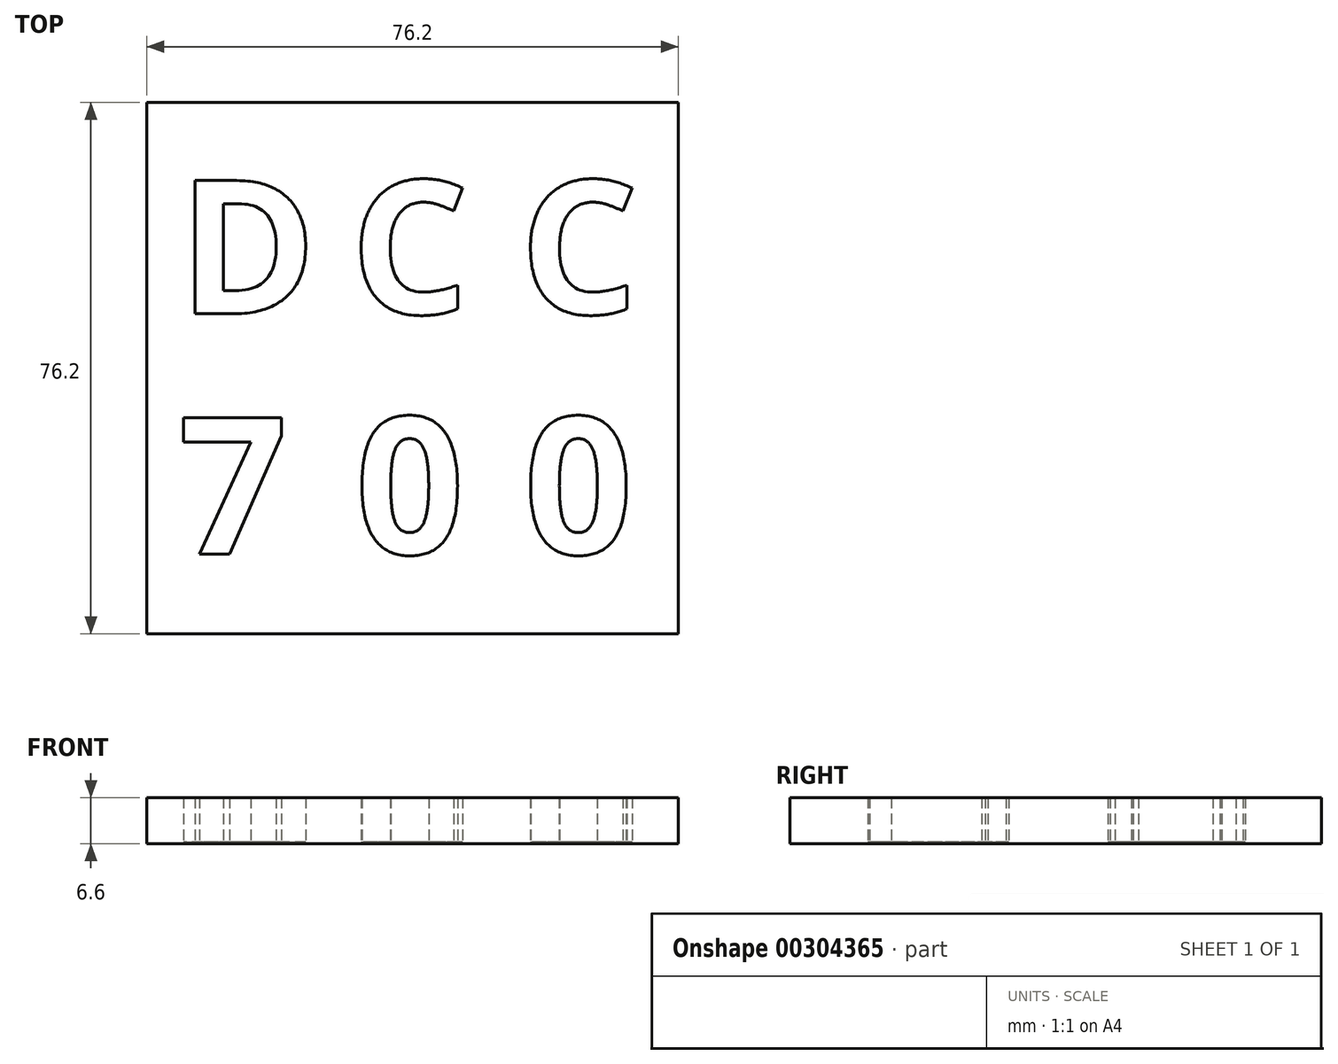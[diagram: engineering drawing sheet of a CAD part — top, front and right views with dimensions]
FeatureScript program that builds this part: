
annotation { "Feature Type Name" : "Feature", "Feature Type Description" : "" }
export const myFeature = defineFeature(function(context is Context, id is Id, definition is map)
    precondition{}
    {
        {
            var Q0;
            Q0=qCreatedBy(makeId("Top.planeOp"),FACE);
            var sketch = newSketch(context, id + "F0", { "sketchPlane" : qUnion([Q0])});
            skLineSegment(sketch, "E0.bottom", {"start": v(-38.1, 38.1) * mm, "end": v(38.1, 38.1) * mm});
            skLineSegment(sketch, "E0.top", {"start": v(-38.1, -38.1) * mm, "end": v(38.1, -38.1) * mm});
            skLineSegment(sketch, "E0.left", {"start": v(-38.1, 38.1) * mm, "end": v(-38.1, -38.1) * mm});
            skLineSegment(sketch, "E0.right", {"start": v(38.1, 38.1) * mm, "end": v(38.1, -38.1) * mm});
            skPoint(sketch, "E0.middle", {"position": v(0, 0) * mm});
            skText(sketch, "E1", { "text": "D\n", "fontName": "OpenSans-Bold.ttf"});
            skText(sketch, "E2", { "text": "C", "fontName": "OpenSans-Bold.ttf"});
            skText(sketch, "E3", { "text": "C\n", "fontName": "OpenSans-Bold.ttf"});
            skText(sketch, "E4", { "text": "7", "fontName": "OpenSans-Bold.ttf"});
            skText(sketch, "E5", { "text": "0", "fontName": "OpenSans-Bold.ttf"});
            skText(sketch, "E6", { "text": "0", "fontName": "OpenSans-Bold.ttf"});
            const initialGuessF0  = {"E1": [-0.03359, 0.00778, 1, 0, 0.01927], "E2": [-0.00892, 0.00778, 1, 0, 0.01927], "E3": [0.01535, 0.00778, 1, 0, 0.01927], "E4": [-0.03359, -0.02666, 1, 0, 0.01976], "E5": [-0.00824, -0.02666, 1, 0, 0.01976], "E6": [0.01594, -0.02666, 1, 0, 0.01976]};
            skSetInitialGuess(sketch, initialGuessF0);
            skSolve(sketch);
        }
        {
            var Q0;
            Q0 = qSketchRegion(id + "F0", true);
            var Q1;
            Q1=makeQuery(id+"F0.imprint","IMPRINT",FACE,{"disambiguationData":[TD([[makeQuery(id+"F0.imprint","IMPRINT",EDGE,{"derivedFrom":sQuery(id+"F0.wireOp",EDGE,"E1.sketch_text.stroke-7")}),1.0]])]});
            var Q2;
            Q2=makeQuery(id+"F0.imprint","IMPRINT",FACE,{"disambiguationData":[TD([[makeQuery(id+"F0.imprint","IMPRINT",EDGE,{"derivedFrom":sQuery(id+"F0.wireOp",EDGE,"E5.sketch_text.stroke-8")}),1.0]])]});
            var Q3;
            Q3=makeQuery(id+"F0.imprint","IMPRINT",FACE,{"disambiguationData":[TD([[makeQuery(id+"F0.imprint","IMPRINT",EDGE,{"derivedFrom":sQuery(id+"F0.wireOp",EDGE,"E6.sketch_text.stroke-8")}),1.0]])]});
            extrude(context, id + "F1", {"entities" : qUnion([Q0, Q1, Q2, Q3]), "depth" : 6.35 * mm});
        }
        {
            var Q0;
            Q0=makeQuery(id+"F1.opExtrude","CAP_FACE",FACE,{"disambiguationData":[OSD([sQuery(id+"F0.wireOp",EDGE,"E0.bottom"),sQuery(id+"F0.wireOp",EDGE,"E0.top"),sQuery(id+"F0.wireOp",EDGE,"E0.left"),sQuery(id+"F0.wireOp",EDGE,"E0.right"),sQuery(id+"F0.wireOp",EDGE,"E1.sketch_text.stroke-0"),sQuery(id+"F0.wireOp",EDGE,"E1.sketch_text.stroke-1"),sQuery(id+"F0.wireOp",EDGE,"E1.sketch_text.stroke-2"),sQuery(id+"F0.wireOp",EDGE,"E1.sketch_text.stroke-3"),sQuery(id+"F0.wireOp",EDGE,"E1.sketch_text.stroke-4"),sQuery(id+"F0.wireOp",EDGE,"E1.sketch_text.stroke-5"),sQuery(id+"F0.wireOp",EDGE,"E1.sketch_text.stroke-6"),sQuery(id+"F0.wireOp",EDGE,"E2.sketch_text.stroke-0"),sQuery(id+"F0.wireOp",EDGE,"E2.sketch_text.stroke-1"),sQuery(id+"F0.wireOp",EDGE,"E2.sketch_text.stroke-2"),sQuery(id+"F0.wireOp",EDGE,"E2.sketch_text.stroke-3"),sQuery(id+"F0.wireOp",EDGE,"E2.sketch_text.stroke-4"),sQuery(id+"F0.wireOp",EDGE,"E2.sketch_text.stroke-5"),sQuery(id+"F0.wireOp",EDGE,"E2.sketch_text.stroke-6"),sQuery(id+"F0.wireOp",EDGE,"E2.sketch_text.stroke-7"),sQuery(id+"F0.wireOp",EDGE,"E2.sketch_text.stroke-8"),sQuery(id+"F0.wireOp",EDGE,"E2.sketch_text.stroke-9"),sQuery(id+"F0.wireOp",EDGE,"E2.sketch_text.stroke-10"),sQuery(id+"F0.wireOp",EDGE,"E2.sketch_text.stroke-11"),sQuery(id+"F0.wireOp",EDGE,"E2.sketch_text.stroke-12"),sQuery(id+"F0.wireOp",EDGE,"E2.sketch_text.stroke-13"),sQuery(id+"F0.wireOp",EDGE,"E2.sketch_text.stroke-14"),sQuery(id+"F0.wireOp",EDGE,"E3.sketch_text.stroke-0"),sQuery(id+"F0.wireOp",EDGE,"E3.sketch_text.stroke-1"),sQuery(id+"F0.wireOp",EDGE,"E3.sketch_text.stroke-2"),sQuery(id+"F0.wireOp",EDGE,"E3.sketch_text.stroke-3"),sQuery(id+"F0.wireOp",EDGE,"E3.sketch_text.stroke-4"),sQuery(id+"F0.wireOp",EDGE,"E3.sketch_text.stroke-5"),sQuery(id+"F0.wireOp",EDGE,"E3.sketch_text.stroke-6"),sQuery(id+"F0.wireOp",EDGE,"E3.sketch_text.stroke-7"),sQuery(id+"F0.wireOp",EDGE,"E3.sketch_text.stroke-8"),sQuery(id+"F0.wireOp",EDGE,"E3.sketch_text.stroke-9"),sQuery(id+"F0.wireOp",EDGE,"E3.sketch_text.stroke-10"),sQuery(id+"F0.wireOp",EDGE,"E3.sketch_text.stroke-11"),sQuery(id+"F0.wireOp",EDGE,"E3.sketch_text.stroke-12"),sQuery(id+"F0.wireOp",EDGE,"E3.sketch_text.stroke-13"),sQuery(id+"F0.wireOp",EDGE,"E3.sketch_text.stroke-14"),sQuery(id+"F0.wireOp",EDGE,"E4.sketch_text.stroke-0"),sQuery(id+"F0.wireOp",EDGE,"E4.sketch_text.stroke-1"),sQuery(id+"F0.wireOp",EDGE,"E4.sketch_text.stroke-2"),sQuery(id+"F0.wireOp",EDGE,"E4.sketch_text.stroke-3"),sQuery(id+"F0.wireOp",EDGE,"E4.sketch_text.stroke-4"),sQuery(id+"F0.wireOp",EDGE,"E4.sketch_text.stroke-5"),sQuery(id+"F0.wireOp",EDGE,"E4.sketch_text.stroke-6"),sQuery(id+"F0.wireOp",EDGE,"E5.sketch_text.stroke-0"),sQuery(id+"F0.wireOp",EDGE,"E5.sketch_text.stroke-1"),sQuery(id+"F0.wireOp",EDGE,"E5.sketch_text.stroke-2"),sQuery(id+"F0.wireOp",EDGE,"E5.sketch_text.stroke-3"),sQuery(id+"F0.wireOp",EDGE,"E5.sketch_text.stroke-4"),sQuery(id+"F0.wireOp",EDGE,"E5.sketch_text.stroke-5"),sQuery(id+"F0.wireOp",EDGE,"E5.sketch_text.stroke-6"),sQuery(id+"F0.wireOp",EDGE,"E5.sketch_text.stroke-7"),sQuery(id+"F0.wireOp",EDGE,"E6.sketch_text.stroke-0"),sQuery(id+"F0.wireOp",EDGE,"E6.sketch_text.stroke-1"),sQuery(id+"F0.wireOp",EDGE,"E6.sketch_text.stroke-2"),sQuery(id+"F0.wireOp",EDGE,"E6.sketch_text.stroke-3"),sQuery(id+"F0.wireOp",EDGE,"E6.sketch_text.stroke-4"),sQuery(id+"F0.wireOp",EDGE,"E6.sketch_text.stroke-5"),sQuery(id+"F0.wireOp",EDGE,"E6.sketch_text.stroke-6"),sQuery(id+"F0.wireOp",EDGE,"E6.sketch_text.stroke-7")])],"isStart":true});
            var sketch = newSketch(context, id + "F2", { "sketchPlane" : qUnion([Q0])});
            skLineSegment(sketch, "E7.bottom", {"start": v(38.1, -38.1) * mm, "end": v(-38.1, -38.1) * mm});
            skLineSegment(sketch, "E7.top", {"start": v(38.1, 38.1) * mm, "end": v(-38.1, 38.1) * mm});
            skLineSegment(sketch, "E7.left", {"start": v(38.1, -38.1) * mm, "end": v(38.1, 38.1) * mm});
            skLineSegment(sketch, "E7.right", {"start": v(-38.1, -38.1) * mm, "end": v(-38.1, 38.1) * mm});
            skPoint(sketch, "E7.middle", {"position": v(0, 0) * mm});
            skSolve(sketch);
        }
        {
            var Q0;
            Q0 = qSketchRegion(id + "F2", true);
            extrude(context, id + "F3", {"entities" : qUnion([Q0]), "operationType" : NewBodyOperationType.ADD, "depth" : 0.25 * mm});
        }
    });
